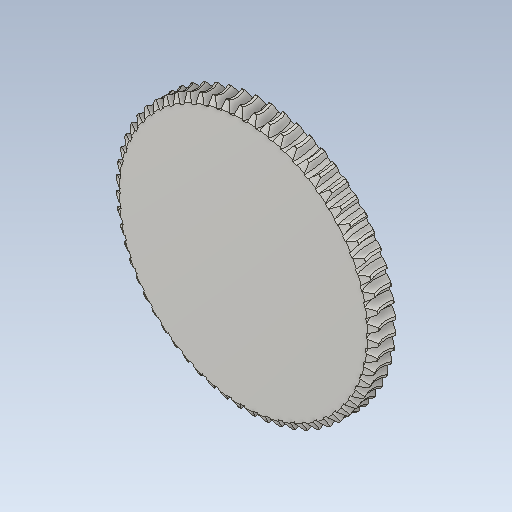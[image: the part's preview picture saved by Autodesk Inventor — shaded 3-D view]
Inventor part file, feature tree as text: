
AUTODESK INVENTOR PART (.ipt)
format: ipt  version: 2021.1 (Build 251245010, 245A)  size: 1,135,616 bytes
history: native  units: mm (DEFAULTED — no unit token found)
features: other x8, plane x3, pattern_circular x1, sketch x1
ambient origin geometry x5: Origin, X Axis, Y Axis, Z Axis, Center Point
bodies: Solid1 (feature_tree)
feature tree (13):
  other  "Tooth Plane"
  other  "Base Body Sketch"
  other  "Base Body"
  other  "Base Body2"
  plane  "Work Plane13"
  other  "Tooth"
  pattern_circular  "Tooth Pattern"  [2 undecoded]
  plane  "Work Plane14"
  plane  "Work Plane15"
  other  "Tooth Sketch"
  sketch  "Sketch8"  dims[d35=90.0deg d37=-0.996687mm d38=70.744372mm d39=3.490659mm d40=7.680818mm d41=10.106339mm d42=1.905mm d43=90.0deg d44=600.0mm d46=360.0deg d50=5.318254mm d68=70.744372mm d69=0.0mm d73=0.0mm d75=0.523599mm d77=121.276067mm d78=12.3mm d79=0.0mm d80=0.0mm d81=0.0mm d82=0.0mm d83=0.523599mm d84=0.0mm d85=180.0deg d86=70.744372mm d87=127.33987mm d89=16.170142mm d90=90.0deg d92=12.3mm d93=70.744372mm]
  other  "Srf1"
  other  "Pitch Diameter"
note: 2 required parameter values undecoded (feature->parameter linkage not recoverable at this tier; creation-order binding heuristic only, values carry confidence <= 0.55)
